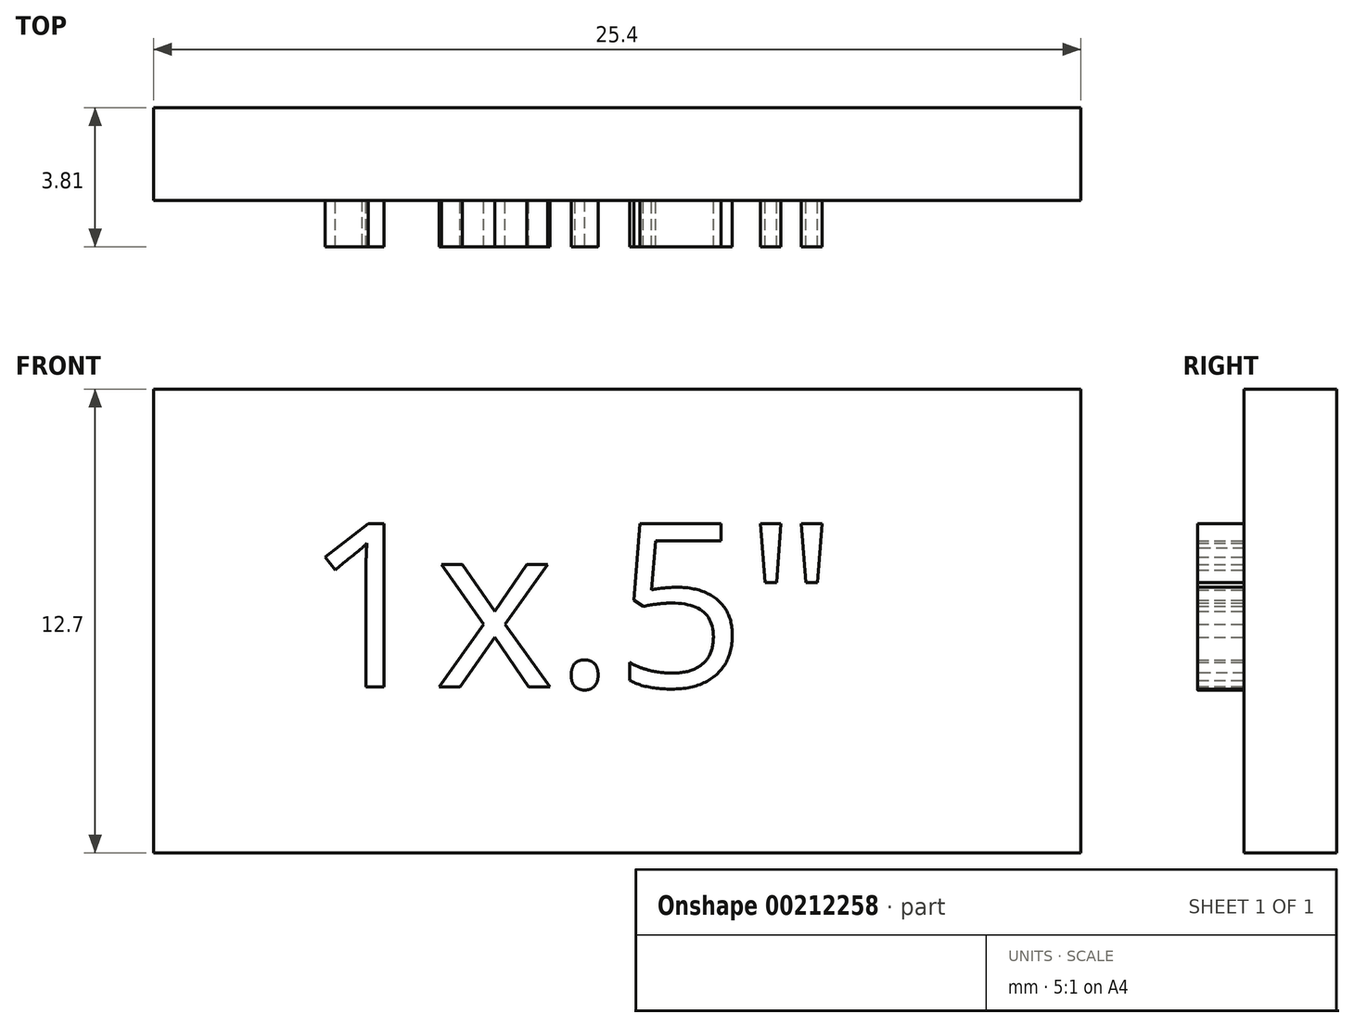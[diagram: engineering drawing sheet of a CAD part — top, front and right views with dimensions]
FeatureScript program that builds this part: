
annotation { "Feature Type Name" : "Feature", "Feature Type Description" : "" }
export const myFeature = defineFeature(function(context is Context, id is Id, definition is map)
    precondition{}
    {
        {
            var Q0;
            Q0=qCreatedBy(makeId("Front.planeOp"),FACE);
            var sketch = newSketch(context, id + "F0", { "sketchPlane" : qUnion([Q0])});
            skLineSegment(sketch, "E0.bottom", {"start": v(-32.73, 17.54) * mm, "end": v(-7.33, 17.54) * mm});
            skLineSegment(sketch, "E0.top", {"start": v(-32.73, 4.84) * mm, "end": v(-7.33, 4.84) * mm});
            skLineSegment(sketch, "E0.left", {"start": v(-32.73, 17.54) * mm, "end": v(-32.73, 4.84) * mm});
            skLineSegment(sketch, "E0.right", {"start": v(-7.33, 17.54) * mm, "end": v(-7.33, 4.84) * mm});
            skSolve(sketch);
        }
        {
            var Q0;
            Q0=makeQuery(id+"F0.imprint","IMPRINT",FACE,{"disambiguationData":[TD([[makeQuery(id+"F0.imprint","IMPRINT",EDGE,{"derivedFrom":sQuery(id+"F0.wireOp",EDGE,"E0.bottom")}),-1.0]])]});
            extrude(context, id + "F1", {"entities" : qUnion([Q0]), "depth" : 2.54 * mm});
        }
        {
            var Q0;
            Q0=makeQuery(id+"F1.opExtrude","CAP_FACE",FACE,{"disambiguationData":[OSD([sQuery(id+"F0.wireOp",EDGE,"E0.bottom"),sQuery(id+"F0.wireOp",EDGE,"E0.top"),sQuery(id+"F0.wireOp",EDGE,"E0.left"),sQuery(id+"F0.wireOp",EDGE,"E0.right")])],"isStart":false});
            var sketch = newSketch(context, id + "F2", { "sketchPlane" : qUnion([Q0])});
            skText(sketch, "E1", { "text": "1x.5\"", "fontName": "OpenSans-Regular.ttf"});
            const initialGuessF2  = {"E1": [-0.0286, 0.00939, 1, 0, 0.0045]};
            skSetInitialGuess(sketch, initialGuessF2);
            skSolve(sketch);
        }
        {
            var Q0;
            Q0 = qSketchRegion(id + "F2", true);
            extrude(context, id + "F3", {"entities" : qUnion([Q0]), "operationType" : NewBodyOperationType.ADD, "depth" : 1.27 * mm});
        }
    });
